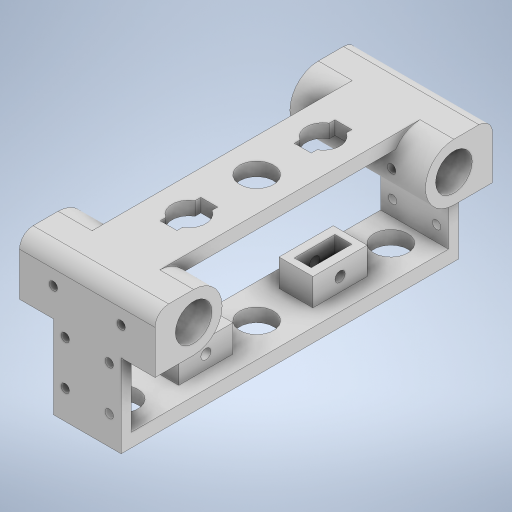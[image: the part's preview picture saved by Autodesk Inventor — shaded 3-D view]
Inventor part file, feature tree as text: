
AUTODESK INVENTOR PART (.ipt)
format: ipt  version: 2024 (Build 280153000, 153)  size: 528,896 bytes
history: native  units: mm
features: extrude x11, sketch x10, projected_geometry x8, other x1, fillet x1
ambient origin geometry x8: Origin, YZ Plane, XZ Plane, XY Plane, X Axis, Y Axis, Z Axis, Center Point
bodies: Body1 (feature_tree)
feature tree (31):
  other  "솔리드1"
  extrude  "돌출1"  Depth=30.0mm
  fillet  "모깎기1"  Radius=3.0mm
  extrude  "돌출4"  Depth=20.0mm TaperAngle=0.0deg
  extrude  "돌출5"  Depth=10.8mm
  sketch  "스케치6"
  extrude  "돌출6"  Depth=16.8mm
  extrude  "돌출7"  Depth=8.5mm
  extrude  "돌출8"  Depth=3.0mm
  extrude  "돌출9"  Depth=38.4mm
  sketch  "스케치9"
  extrude  "돌출10"  Depth=4.0mm
  sketch  "스케치11"
  extrude  "돌출20"  Depth=2.5mm
  extrude  "돌출21"  Depth=8.5mm
  extrude  "돌출22"  Depth=3.5mm
  sketch  "스케치1"
  sketch  "스케치4"
  sketch  "스케치5"
  projected_geometry  "투영된 루프1"
  projected_geometry  "투영된 루프2"
  sketch  "스케치7"
  sketch  "스케치8"
  projected_geometry  "투영된 루프3"
  projected_geometry  "투영된 루프4"
  sketch  "스케치10"
  projected_geometry  "투영된 루프5"
  projected_geometry  "투영된 루프6"
  sketch  "스케치16"
  projected_geometry  "투영된 루프9"
  projected_geometry  "투영된 루프10"
